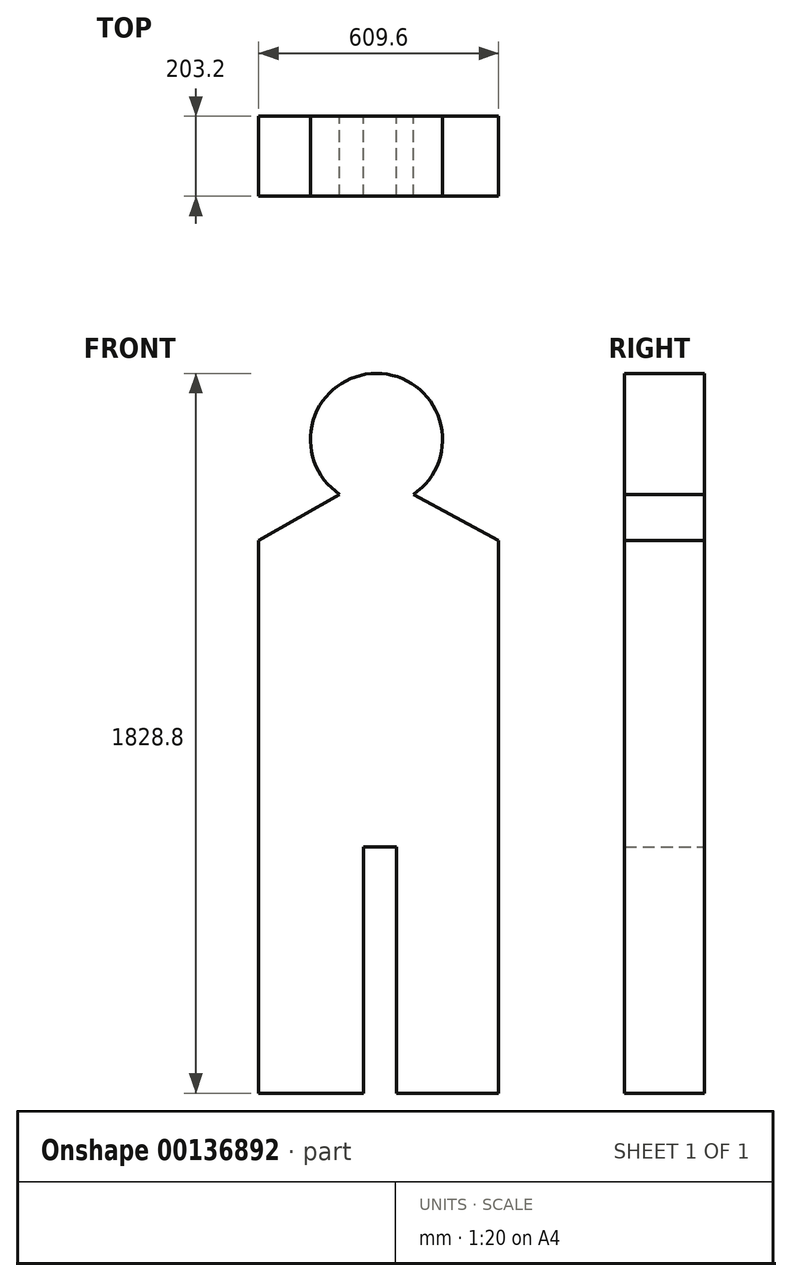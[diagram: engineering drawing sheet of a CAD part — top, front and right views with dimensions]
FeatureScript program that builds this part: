
annotation { "Feature Type Name" : "Feature", "Feature Type Description" : "" }
export const myFeature = defineFeature(function(context is Context, id is Id, definition is map)
    precondition{}
    {
        {
            var Q0;
            Q0=qCreatedBy(makeId("Front.planeOp"),FACE);
            var sketch = newSketch(context, id + "F0", { "sketchPlane" : qUnion([Q0])});
            skLineSegment(sketch, "E0.bottom", {"start": v(-299.04, 908.78) * mm, "end": v(310.56, 908.78) * mm});
            skLineSegment(sketch, "E0.top", {"start": v(-299.04, -920.02) * mm, "end": v(310.56, -920.02) * mm});
            skLineSegment(sketch, "E0.left", {"start": v(-299.04, 908.78) * mm, "end": v(-299.04, -920.02) * mm});
            skLineSegment(sketch, "E0.right", {"start": v(310.56, 908.78) * mm, "end": v(310.56, -920.02) * mm});
            skCircle(sketch, "E1", {"center": v(0, 740.89) * mm, "radius": 167.9 * mm});
            skLineSegment(sketch, "E2", {"start": v(-299.04, 484.03) * mm, "end": v(-93.43, 601.4) * mm});
            skLineSegment(sketch, "E3", {"start": v(93.71, 601.58) * mm, "end": v(310.56, 484.03) * mm});
            skLineSegment(sketch, "E4.bottom", {"start": v(-33.23, -920.02) * mm, "end": v(51.48, -920.02) * mm});
            skLineSegment(sketch, "E4.top", {"start": v(-33.23, -294.73) * mm, "end": v(51.48, -294.73) * mm});
            skLineSegment(sketch, "E4.left", {"start": v(-33.23, -920.02) * mm, "end": v(-33.23, -294.73) * mm});
            skLineSegment(sketch, "E4.right", {"start": v(51.48, -920.02) * mm, "end": v(51.48, -294.73) * mm});
            skSolve(sketch);
        }
        {
            var Q0;
            {var subQ0=sQuery(id+"F0.wireOp",EDGE,"E1");var subQ1=makeQuery(id+"F0.imprint","INTERSECT",VERTEX,{"derivedFrom":[subQ0,sQuery(id+"F0.wireOp",EDGE,"E2")]});Q0=makeQuery(id+"F0.imprint","IMPRINT",FACE,{"disambiguationData":[TD([[makeQuery(id+"F0.imprint","IMPRINT",EDGE,{"disambiguationData":[TD([[subQ1,1.0]])],"derivedFrom":subQ0}),1.0]])]});}
            var Q1;
            {var subQ6=sQuery(id+"F0.wireOp",EDGE,"E2");Q1=makeQuery(id+"F0.imprint","IMPRINT",FACE,{"disambiguationData":[TD([[makeQuery(id+"F0.imprint","IMPRINT",EDGE,{"derivedFrom":subQ6}),-1.0]])]});}
            extrude(context, id + "F1", {"entities" : qUnion([Q0, Q1]), "depth" : 203.2 * mm});
        }
    });
